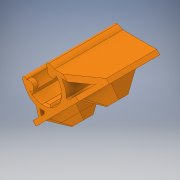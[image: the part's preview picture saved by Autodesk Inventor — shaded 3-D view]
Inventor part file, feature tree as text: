
AUTODESK INVENTOR PART (.ipt)
format: ipt  version: 2017 (Build 210142000, 142)  size: 1,050,112 bytes
history: native  units: in
note: dims shown in document units (in); Inventor stores cm internally (conversion verified against a paired STEP export)
features: extrude x3, sketch x3, other x2
ambient origin geometry x8: Origin, YZ Plane, XZ Plane, XY Plane, X Axis, Y Axis, Z Axis, Center Point
bodies: Solid1 (feature_tree)
feature tree (8):
  other  "10_Support plateau.STEP"
  extrude  "Extrusion1"  TaperAngle=0.0deg  [1 undecoded]
  extrude  "Extrusion3"  [1 undecoded]
  extrude  "Extrusion4"  [1 undecoded]
  sketch  "Sketch1"  dims[d0=0.3937in d1=0.0in d4=0.0in d5=0.0in]
  sketch  "Sketch3"  dims[d6=0.0in d7=0.0in]
  sketch  "Sketch4"
  parser-record x1  (decoder bookkeeping rows leaked as tree rows — omitted from the tree; the rows remain in map.json)
note: 3 required parameter values undecoded (feature->parameter linkage not recoverable at this tier; creation-order binding heuristic only, values carry confidence <= 0.55)
